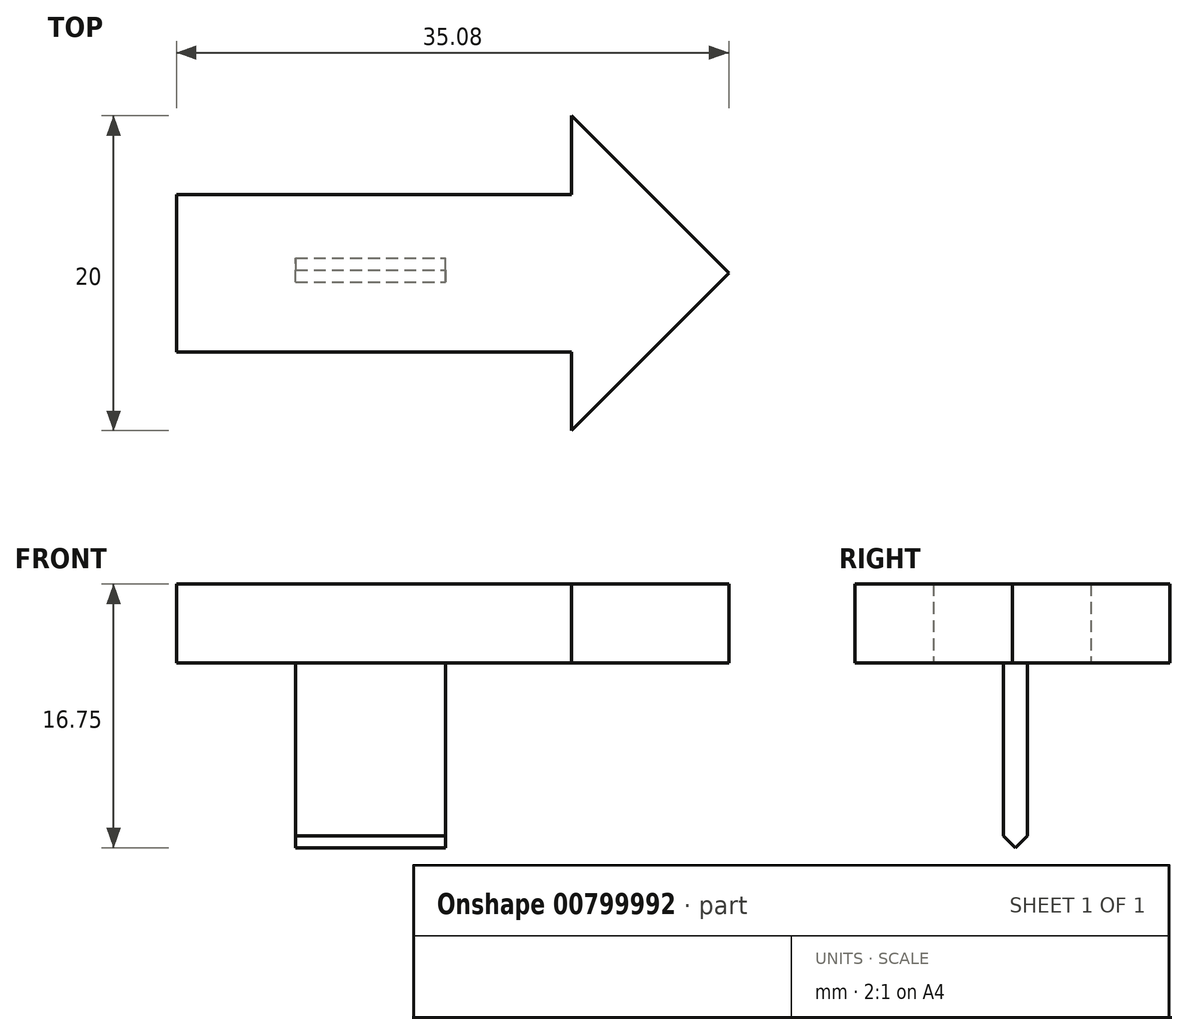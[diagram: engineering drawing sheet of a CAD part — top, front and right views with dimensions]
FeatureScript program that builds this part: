
annotation { "Feature Type Name" : "Feature", "Feature Type Description" : "" }
export const myFeature = defineFeature(function(context is Context, id is Id, definition is map)
    precondition{}
    {
        {
            var Q0;
            Q0=qCreatedBy(makeId("Top.planeOp"),FACE);
            var sketch = newSketch(context, id + "F0", { "sketchPlane" : qUnion([Q0])});
            skLineSegment(sketch, "E0.bottom", {"start": v(-27.64, 5) * mm, "end": v(-2.56, 5) * mm});
            skLineSegment(sketch, "E0.top", {"start": v(-27.64, -5) * mm, "end": v(-2.56, -5) * mm});
            skLineSegment(sketch, "E0.left", {"start": v(-27.64, 5) * mm, "end": v(-27.64, -5) * mm});
            skLineSegment(sketch, "E1", {"start": v(-2.56, 5) * mm, "end": v(-2.56, 10) * mm});
            skLineSegment(sketch, "E2", {"start": v(-2.56, 10) * mm, "end": v(7.44, 0) * mm});
            skLineSegment(sketch, "E3", {"start": v(7.44, 0) * mm, "end": v(-2.56, -10) * mm});
            skLineSegment(sketch, "E4", {"start": v(-2.56, -10) * mm, "end": v(-2.56, -5) * mm});
            skSolve(sketch);
        }
        {
            var Q0;
            Q0 = qSketchRegion(id + "F0", true);
            extrude(context, id + "F1", {"entities" : qUnion([Q0]), "depth" : 5 * mm, "offsetDistance" : 25 * mm});
        }
        {
            var Q0;
            Q0=makeQuery(id+"F1.opExtrude","CAP_FACE",FACE,{"disambiguationData":[OSD([sQuery(id+"F0.wireOp",EDGE,"E0.bottom"),sQuery(id+"F0.wireOp",EDGE,"E0.top"),sQuery(id+"F0.wireOp",EDGE,"E0.left"),sQuery(id+"F0.wireOp",EDGE,"E1"),sQuery(id+"F0.wireOp",EDGE,"E2"),sQuery(id+"F0.wireOp",EDGE,"E3"),sQuery(id+"F0.wireOp",EDGE,"E4")])],"isStart":true});
            var sketch = newSketch(context, id + "F2", { "sketchPlane" : qUnion([Q0])});
            skLineSegment(sketch, "E5.bottom", {"start": v(-20.07, 0.55) * mm, "end": v(-10.57, 0.55) * mm});
            skLineSegment(sketch, "E5.top", {"start": v(-20.07, -0.95) * mm, "end": v(-10.57, -0.95) * mm});
            skLineSegment(sketch, "E5.left", {"start": v(-20.07, 0.55) * mm, "end": v(-20.07, -0.95) * mm});
            skLineSegment(sketch, "E5.right", {"start": v(-10.57, 0.55) * mm, "end": v(-10.57, -0.95) * mm});
            skSolve(sketch);
        }
        {
            var Q0;
            Q0 = qSketchRegion(id + "F2", true);
            extrude(context, id + "F3", {"entities" : qUnion([Q0]), "operationType" : NewBodyOperationType.ADD, "depth" : 12 * mm, "offsetDistance" : 25 * mm});
        }
        {
            var Q0;
            Q0=makeQuery(id+"F3.opExtrude","CAP_EDGE",EDGE,{"disambiguationData":[OSD([sQuery(id+"F2.wireOp",EDGE,"E5.top")])],"isStart":false});
            var Q1;
            Q1=makeQuery(id+"F3.opExtrude","CAP_EDGE",EDGE,{"disambiguationData":[OSD([sQuery(id+"F2.wireOp",EDGE,"E5.bottom")])],"isStart":false});
            chamfer(context, id + "F4", {"entities" : qUnion([Q0, Q1]), "width" : 1 * mm, "tangentPropagation" : true});
        }
    });
